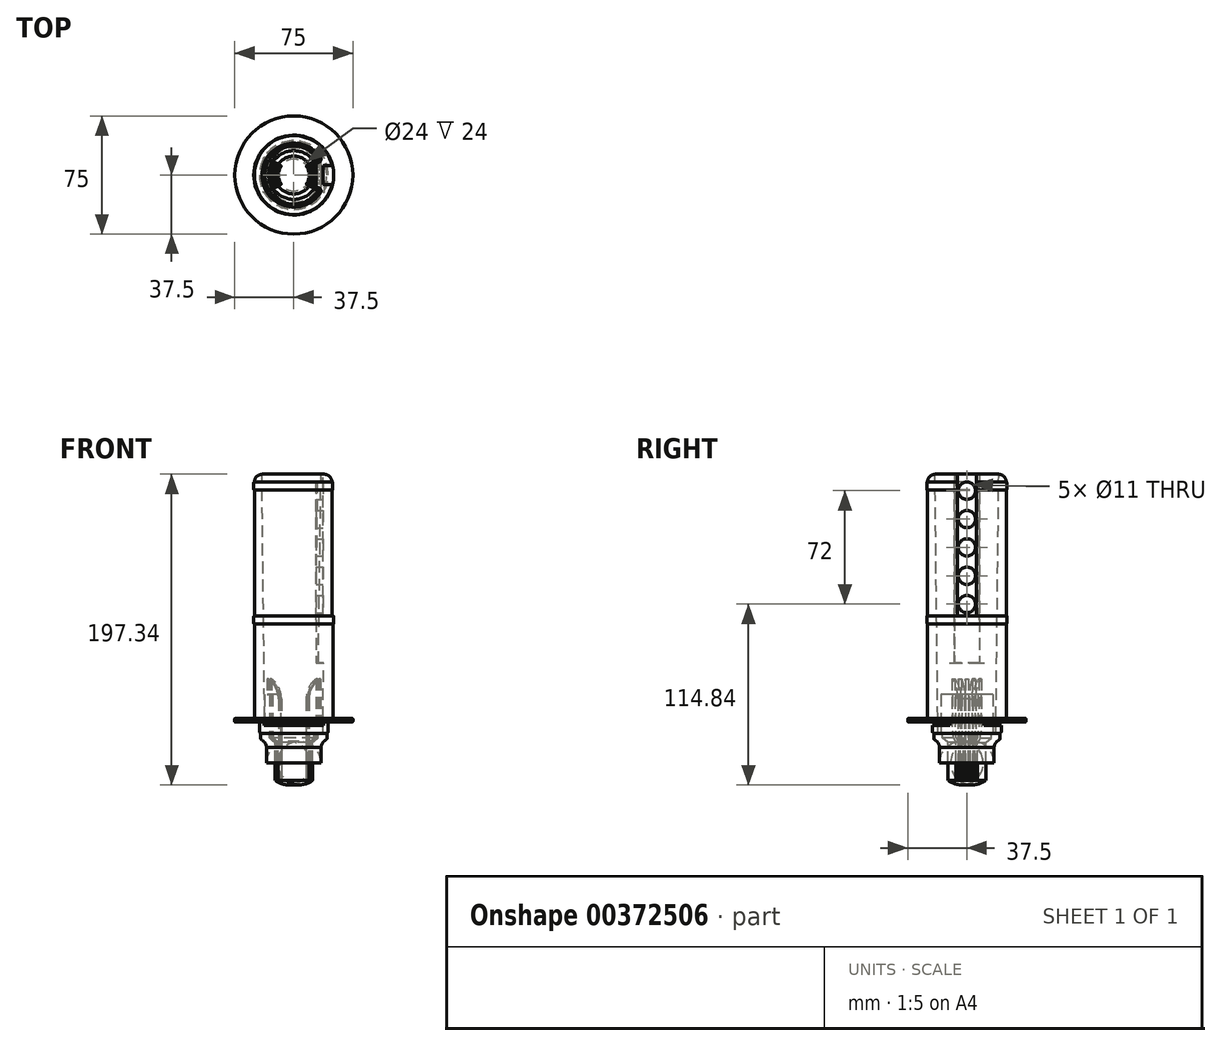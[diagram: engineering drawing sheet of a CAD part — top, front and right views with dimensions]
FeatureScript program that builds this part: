
annotation { "Feature Type Name" : "Feature", "Feature Type Description" : "" }
export const myFeature = defineFeature(function(context is Context, id is Id, definition is map)
    precondition{}
    {
        {
            var Q0;
            Q0=qCreatedBy(makeId("Front.planeOp"),FACE);
            var sketch = newSketch(context, id + "F0", { "sketchPlane" : qUnion([Q0])});
            skLineSegment(sketch, "E0", {"start": v(0, 155) * mm, "end": v(0, -40) * mm});
            skLineSegment(sketch, "E1", {"start": v(0, 155) * mm, "end": v(25, 155) * mm});
            skLineSegment(sketch, "E2", {"start": v(25, 155) * mm, "end": v(25, 150) * mm});
            skLineSegment(sketch, "E3", {"start": v(25, 150) * mm, "end": v(25.4, 150) * mm});
            skLineSegment(sketch, "E4", {"start": v(25.4, 150) * mm, "end": v(25.4, 145) * mm});
            skLineSegment(sketch, "E5", {"start": v(25.4, 145) * mm, "end": v(25, 145) * mm});
            skLineSegment(sketch, "E6", {"start": v(25, 145) * mm, "end": v(25, 65) * mm});
            skLineSegment(sketch, "E7", {"start": v(25, 65) * mm, "end": v(25.4, 65) * mm});
            skLineSegment(sketch, "E8", {"start": v(25.4, 65) * mm, "end": v(25.4, 60) * mm});
            skLineSegment(sketch, "E9", {"start": v(25.4, 60) * mm, "end": v(25, 60) * mm});
            skLineSegment(sketch, "E10", {"start": v(25, 60) * mm, "end": v(25, 0) * mm});
            skLineSegment(sketch, "E11", {"start": v(25, 0) * mm, "end": v(27.5, 0) * mm});
            skLineSegment(sketch, "E12", {"start": v(27.5, 0) * mm, "end": v(27.5, -2.5) * mm});
            skLineSegment(sketch, "E13", {"start": v(27.5, -2.5) * mm, "end": v(19.5, -2.5) * mm});
            skLineSegment(sketch, "E14", {"start": v(19.5, -2.5) * mm, "end": v(19.5, -4.5) * mm});
            skLineSegment(sketch, "E15", {"start": v(19.5, -4.5) * mm, "end": v(21.8, -4.5) * mm});
            skLineSegment(sketch, "E16", {"start": v(21.8, -4.5) * mm, "end": v(21.8, -9.5) * mm});
            skLineSegment(sketch, "E17", {"start": v(21.8, -9.5) * mm, "end": v(21, -9.5) * mm});
            skLineSegment(sketch, "E18", {"start": v(21, -9.5) * mm, "end": v(21, -13.5) * mm});
            skLineSegment(sketch, "E19", {"start": v(17.3, -18.5) * mm, "end": v(17.3, -28.5) * mm});
            skLineSegment(sketch, "E20", {"start": v(12, -39.39) * mm, "end": v(0, -39.39) * mm});
            skArc(sketch, "E21", {"start": v(21, -13.5) * mm, "mid": v(18.43, -15.47) * mm, "end": v(17.3, -18.5) * mm});
            skPoint(sketch, "E22.orphan", {"position": v(17.3, -13.5) * mm});
            skPoint(sketch, "E23.start.orphan", {"position": v(12, -28.39) * mm});
            skLineSegment(sketch, "E24", {"start": v(0, 155) * mm, "end": v(20.25, 155) * mm});
            skLineSegment(sketch, "E25", {"start": v(20.25, 155) * mm, "end": v(18.5, 0) * mm});
            skLineSegment(sketch, "E26", {"start": v(18.5, 0) * mm, "end": v(18.5, -10) * mm});
            skLineSegment(sketch, "E27", {"start": v(12, -39.39) * mm, "end": v(12, -15.39) * mm});
            skLineSegment(sketch, "E28", {"start": v(12, -15.39) * mm, "end": v(15.5, -12.49) * mm});
            skArc(sketch, "E29", {"start": v(12, -39.39) * mm, "mid": v(15.9, -34.56) * mm, "end": v(17.3, -28.5) * mm});
            skLineSegment(sketch, "E30", {"start": v(18.5, -10) * mm, "end": v(15.5, -10) * mm});
            skLineSegment(sketch, "E31", {"start": v(15.5, -10) * mm, "end": v(15.5, -12.49) * mm});
            skLineSegment(sketch, "E32", {"start": v(12, -39.39) * mm, "end": v(42.32, -39.39) * mm});
            skLineSegment(sketch, "E33", {"start": v(42.32, -39.39) * mm, "end": v(42.32, -10.56) * mm});
            skLineSegment(sketch, "E34", {"start": v(42.32, -10.56) * mm, "end": v(21, -10.56) * mm});
            skLineSegment(sketch, "E35", {"start": v(27.5, 0) * mm, "end": v(37.5, 0) * mm});
            skLineSegment(sketch, "E36", {"start": v(37.5, 0) * mm, "end": v(37.5, -2.5) * mm});
            skLineSegment(sketch, "E37", {"start": v(37.5, -2.5) * mm, "end": v(27.5, -2.5) * mm});
            skSolve(sketch);
        }
        {
            var Q0;
            {var subQ5=sQuery(id+"F0.wireOp",EDGE,"E2");Q0=makeQuery(id+"F0.imprint","IMPRINT",FACE,{"disambiguationData":[TD([[makeQuery(id+"F0.imprint","IMPRINT",EDGE,{"derivedFrom":subQ5}),-1.0]])]});}
            var Q1;
            Q1=sQuery(id+"F0.wireOp",EDGE,"E0");
            revolve(context, id + "F1", {"entities" : qUnion([Q0]), "axis" : qUnion([Q1]), "revolveType" : RevolveType.FULL});
        }
        {
            var Q0;
            Q0=makeQuery(id+"F1.opRevolve","SWEPT_FACE",FACE,{"disambiguationData":[OSD([sQuery(id+"F0.wireOp",EDGE,"E30")])]});
            var sketch = newSketch(context, id + "F2", { "sketchPlane" : qUnion([Q0])});
            skArc(sketch, "E38", {"start": v(-8.37, 16.5) * mm, "mid": v(-15.5, 0) * mm, "end": v(-8.37, -16.5) * mm});
            skArc(sketch, "E39", {"start": v(8.37, -16.5) * mm, "mid": v(15.5, 0) * mm, "end": v(8.37, 16.5) * mm});
            skSolve(sketch);
        }
        {
            var Q0;
            {var subQ0=sQuery(id+"F2.wireOp",EDGE,"E38");var subQ1=sQuery(id+"F0.wireOp",EDGE,"E30");var subQ2=makeQuery(id+"F1.opRevolve","SWEPT_EDGE",EDGE,{"disambiguationData":[OSD([sQuery(id+"F0.wireOp",EDGE,"E26"),subQ1])]});var subQ3=makeQuery(id+"F2.imprint","INTERSECT",VERTEX,{"disambiguationData":[OD(0.0)],"derivedFrom":[subQ2,subQ0]});Q0=makeQuery(id+"F2.imprint","IMPRINT",FACE,{"disambiguationData":[TD([[makeQuery(id+"F2.imprint","IMPRINT",EDGE,{"disambiguationData":[TD([[subQ3,-1.0]])],"derivedFrom":subQ0}),-1.0]])]});}
            var Q1;
            {var subQ0=sQuery(id+"F2.wireOp",EDGE,"E39");var subQ1=sQuery(id+"F0.wireOp",EDGE,"E30");var subQ2=makeQuery(id+"F1.opRevolve","SWEPT_EDGE",EDGE,{"disambiguationData":[OSD([sQuery(id+"F0.wireOp",EDGE,"E26"),subQ1])]});var subQ3=makeQuery(id+"F2.imprint","INTERSECT",VERTEX,{"disambiguationData":[OD(0.0)],"derivedFrom":[subQ2,subQ0]});Q1=makeQuery(id+"F2.imprint","IMPRINT",FACE,{"disambiguationData":[TD([[makeQuery(id+"F2.imprint","IMPRINT",EDGE,{"disambiguationData":[TD([[subQ3,-1.0]])],"derivedFrom":subQ0}),-1.0]])]});}
            extrude(context, id + "F3", {"entities" : qUnion([Q0, Q1]), "operationType" : NewBodyOperationType.ADD, "offsetDistance" : 25 * mm, "depth" : 25 * mm});
        }
        {
            var Q0;
            Q0=makeQuery(id+"F0.imprint","IMPRINT",FACE,{"disambiguationData":[TD([[makeQuery(id+"F0.imprint","IMPRINT",EDGE,{"derivedFrom":sQuery(id+"F0.wireOp",EDGE,"E19")}),1.0]])]});
            var Q1;
            Q1=makeQuery(id+"F1.opRevolve","SWEPT_FACE",FACE,{"disambiguationData":[OSD([sQuery(id+"F0.wireOp",EDGE,"E10")])]});
            revolve(context, id + "F4", {"operationType" : NewBodyOperationType.REMOVE, "entities" : qUnion([Q0]), "axis" : qUnion([Q1]), "revolveType" : RevolveType.FULL, "oppositeDirection" : true});
        }
        {
            var Q0;
            Q0=makeQuery(id+"F1.opRevolve","SWEPT_FACE",FACE,{"disambiguationData":[OSD([sQuery(id+"F0.wireOp",EDGE,"E1")])]});
            var sketch = newSketch(context, id + "F5", { "sketchPlane" : qUnion([Q0])});
            skLineSegment(sketch, "E40", {"start": v(25, 0) * mm, "end": v(23.69, 0) * mm});
            skLineSegment(sketch, "E41", {"start": v(14, 0) * mm, "end": v(14, -8) * mm});
            skLineSegment(sketch, "E42", {"start": v(14, -8) * mm, "end": v(23.69, -8) * mm});
            skLineSegment(sketch, "E43", {"start": v(14, 0) * mm, "end": v(14, 8) * mm});
            skLineSegment(sketch, "E44", {"start": v(14, 8) * mm, "end": v(23.69, 8) * mm});
            skLineSegment(sketch, "E45", {"start": v(23.69, 8) * mm, "end": v(23.69, 6) * mm});
            skLineSegment(sketch, "E46", {"start": v(23.69, -6) * mm, "end": v(24.27, -6) * mm});
            skLineSegment(sketch, "E47", {"start": v(23.69, 6) * mm, "end": v(24.27, 6) * mm});
            skLineSegment(sketch, "E48", {"start": v(24.27, -6) * mm, "end": v(26.6, -6) * mm});
            skLineSegment(sketch, "E49", {"start": v(26.6, -6) * mm, "end": v(26.6, 6) * mm});
            skLineSegment(sketch, "E50", {"start": v(26.6, 6) * mm, "end": v(24.27, 6) * mm});
            skLineSegment(sketch, "E51.trimOffspring", {"start": v(23.69, -6) * mm, "end": v(23.69, -8) * mm});
            skLineSegment(sketch, "E52", {"start": v(23.69, -6) * mm, "end": v(20.27, -6) * mm});
            skLineSegment(sketch, "E53", {"start": v(20.27, -6) * mm, "end": v(20.27, 6) * mm});
            skLineSegment(sketch, "E54", {"start": v(20.27, 6) * mm, "end": v(23.69, 6) * mm});
            skSolve(sketch);
        }
        {
            var Q0;
            {var subQ0=sQuery(id+"F5.wireOp",EDGE,"E40");var subQ1=sQuery(id+"F0.wireOp",EDGE,"E1");var subQ2=makeQuery(id+"F1.opRevolve","SWEPT_EDGE",EDGE,{"disambiguationData":[OSD([subQ1,sQuery(id+"F0.wireOp",EDGE,"E2")])]});var subQ3=makeQuery(id+"F5.imprint","INTERSECT",VERTEX,{"derivedFrom":[subQ2,subQ0]});Q0=makeQuery(id+"F5.imprint","IMPRINT",FACE,{"disambiguationData":[TD([[makeQuery(id+"F5.imprint","IMPRINT",EDGE,{"disambiguationData":[TD([[subQ3,-1.0]])],"derivedFrom":subQ0}),-1.0]])]});}
            var Q1;
            {var subQ0=sQuery(id+"F5.wireOp",EDGE,"E43");Q1=makeQuery(id+"F5.imprint","IMPRINT",FACE,{"disambiguationData":[TD([[makeQuery(id+"F5.imprint","IMPRINT",EDGE,{"derivedFrom":subQ0}),-1.0]])]});}
            var Q2;
            {var subQ0=sQuery(id+"F5.wireOp",EDGE,"E41");Q2=makeQuery(id+"F5.imprint","IMPRINT",FACE,{"disambiguationData":[TD([[makeQuery(id+"F5.imprint","IMPRINT",EDGE,{"derivedFrom":subQ0}),1.0]])]});}
            var Q3;
            {var subQ0=sQuery(id+"F5.wireOp",EDGE,"E40");var subQ1=sQuery(id+"F0.wireOp",EDGE,"E1");var subQ2=makeQuery(id+"F1.opRevolve","SWEPT_EDGE",EDGE,{"disambiguationData":[OSD([subQ1,sQuery(id+"F0.wireOp",EDGE,"E2")])]});var subQ3=makeQuery(id+"F5.imprint","INTERSECT",VERTEX,{"derivedFrom":[subQ2,subQ0]});Q3=makeQuery(id+"F5.imprint","IMPRINT",FACE,{"disambiguationData":[TD([[makeQuery(id+"F5.imprint","IMPRINT",EDGE,{"disambiguationData":[TD([[subQ3,-1.0]])],"derivedFrom":subQ0}),1.0]])]});}
            extrude(context, id + "F6", {"entities" : qUnion([Q0, Q1, Q2, Q3]), "operationType" : NewBodyOperationType.ADD, "oppositeDirection" : true, "depth" : 120 * mm});
        }
        {
            var Q0;
            {var subQ3=sQuery(id+"F5.wireOp",EDGE,"E48");Q0=makeQuery(id+"F5.imprint","IMPRINT",FACE,{"disambiguationData":[TD([[makeQuery(id+"F5.imprint","IMPRINT",EDGE,{"derivedFrom":subQ3}),1.0]])]});}
            var Q1;
            {var subQ3=sQuery(id+"F5.wireOp",EDGE,"29Uc3Rk1-qTzH-c9HX-FljC-5hYWEdNYT9Md");Q1=makeQuery(id+"F5.imprint","IMPRINT",FACE,{"disambiguationData":[TD([[makeQuery(id+"F5.imprint","IMPRINT",EDGE,{"derivedFrom":subQ3}),1.0]])]});}
            var Q2;
            {var subQ5=sQuery(id+"F5.wireOp",EDGE,"E47");Q2=makeQuery(id+"F5.imprint","IMPRINT",FACE,{"disambiguationData":[TD([[makeQuery(id+"F5.imprint","IMPRINT",EDGE,{"derivedFrom":subQ5}),-1.0]])]});}
            extrude(context, id + "F7", {"entities" : qUnion([Q0, Q1, Q2]), "operationType" : NewBodyOperationType.REMOVE, "oppositeDirection" : true, "depth" : 90 * mm});
        }
        {
            var Q0;
            Q0=makeQuery(id+"F7.boolean.opBoolean","COPY",FACE,{"derivedFrom":makeQuery(id+"F7.opExtrude","SWEPT_FACE",FACE,{"disambiguationData":[OSD([sQuery(id+"F5.wireOp",EDGE,"E53")])]})});
            var sketch = newSketch(context, id + "F8", { "sketchPlane" : qUnion([Q0])});
            skCircle(sketch, "E55", {"center": v(0, 144.5) * mm, "radius": 5.5 * mm});
            skPoint(sketch, "E56", {"position": v(0, 155) * mm});
            skCircle(sketch, "E57.0.1.0", {"center": v(0, 126.5) * mm, "radius": 5.5 * mm});
            skCircle(sketch, "E57.0.2.0", {"center": v(0, 108.5) * mm, "radius": 5.5 * mm});
            skCircle(sketch, "E57.0.3.0", {"center": v(0, 90.5) * mm, "radius": 5.5 * mm});
            skCircle(sketch, "E57.0.4.0", {"center": v(0, 72.5) * mm, "radius": 5.5 * mm});
            skLineSegment(sketch, "E57.direction1", {"start": v(0, 144.5) * mm, "end": v(25, 144.5) * mm, "construction": true});
            skLineSegment(sketch, "E57.direction2", {"start": v(0, 144.5) * mm, "end": v(0, 126.5) * mm, "construction": true});
            skSolve(sketch);
        }
        {
            var Q0;
            Q0=makeQuery(id+"F8.imprint","IMPRINT",FACE,{"disambiguationData":[TD([[makeQuery(id+"F8.imprint","IMPRINT",EDGE,{"derivedFrom":sQuery(id+"F8.wireOp",EDGE,"E57.0.4.0")}),1.0]])]});
            var Q1;
            Q1=makeQuery(id+"F8.imprint","IMPRINT",FACE,{"disambiguationData":[TD([[makeQuery(id+"F8.imprint","IMPRINT",EDGE,{"derivedFrom":sQuery(id+"F8.wireOp",EDGE,"E57.0.3.0")}),1.0]])]});
            var Q2;
            Q2=makeQuery(id+"F8.imprint","IMPRINT",FACE,{"disambiguationData":[TD([[makeQuery(id+"F8.imprint","IMPRINT",EDGE,{"derivedFrom":sQuery(id+"F8.wireOp",EDGE,"E57.0.2.0")}),1.0]])]});
            var Q3;
            Q3=makeQuery(id+"F8.imprint","IMPRINT",FACE,{"disambiguationData":[TD([[makeQuery(id+"F8.imprint","IMPRINT",EDGE,{"derivedFrom":sQuery(id+"F8.wireOp",EDGE,"E57.0.1.0")}),1.0]])]});
            var Q4;
            Q4=makeQuery(id+"F8.imprint","IMPRINT",FACE,{"disambiguationData":[TD([[makeQuery(id+"F8.imprint","IMPRINT",EDGE,{"derivedFrom":sQuery(id+"F8.wireOp",EDGE,"E55")}),1.0]])]});
            extrude(context, id + "F9", {"entities" : qUnion([Q0, Q1, Q2, Q3, Q4]), "operationType" : NewBodyOperationType.REMOVE, "oppositeDirection" : true, "depth" : 13 * mm, "hasSecondDirection" : true, "secondDirectionOppositeDirection" : false, "secondDirectionDepth" : 3 * mm});
        }
        {
            var Q0;
            Q0=makeQuery(id+"F1.opRevolve","SWEPT_FACE",FACE,{"disambiguationData":[OSD([sQuery(id+"F0.wireOp",EDGE,"E13")])]});
            var sketch = newSketch(context, id + "F10", { "sketchPlane" : qUnion([Q0])});
            skLineSegment(sketch, "E58", {"start": v(-27.5, 0) * mm, "end": v(-15, 0) * mm});
            skLineSegment(sketch, "E59", {"start": v(-15, 0) * mm, "end": v(-15, -11) * mm});
            skLineSegment(sketch, "E60", {"start": v(-15, -11) * mm, "end": v(-19.63, -11) * mm});
            skLineSegment(sketch, "E61", {"start": v(-22.5, -0.5) * mm, "end": v(-22.5, 0) * mm});
            skLineSegment(sketch, "E62", {"start": v(-19.68, 10.9) * mm, "end": v(-15, 11) * mm});
            skLineSegment(sketch, "E63", {"start": v(-15, 11) * mm, "end": v(-15, 0) * mm});
            skLineSegment(sketch, "E64.MirrorCS", {"start": v(15, 11) * mm, "end": v(15, 0) * mm});
            skLineSegment(sketch, "E65.MirrorCS", {"start": v(19.68, 10.9) * mm, "end": v(15, 11) * mm});
            skLineSegment(sketch, "E66.MirrorCS", {"start": v(15, -11) * mm, "end": v(19.63, -11) * mm});
            skLineSegment(sketch, "E67.MirrorCS", {"start": v(15, 0) * mm, "end": v(15, -11) * mm});
            skCircle(sketch, "E68", {"center": v(0, 0) * mm, "radius": 22.5 * mm});
            skCircle(sketch, "E69", {"center": v(0, 0) * mm, "radius": 19.5 * mm});
            skPoint(sketch, "E70.orphan", {"position": v(-22.74, 10.83) * mm});
            skPoint(sketch, "E71.orphan", {"position": v(-22.26, -11) * mm});
            skPoint(sketch, "E72.orphan", {"position": v(22.26, -11) * mm});
            skPoint(sketch, "E73.MirrorCS.end.orphan", {"position": v(22.74, 10.83) * mm});
            skSolve(sketch);
        }
        {
            var Q0;
            {var subQ0=sQuery(id+"F10.wireOp",EDGE,"E68");var subQ1=sQuery(id+"F10.wireOp",EDGE,"E58");var subQ2=makeQuery(id+"F10.imprint","INTERSECT",VERTEX,{"derivedFrom":[subQ1,subQ0]});Q0=makeQuery(id+"F10.imprint","IMPRINT",FACE,{"disambiguationData":[TD([[makeQuery(id+"F10.imprint","IMPRINT",EDGE,{"disambiguationData":[TD([[subQ2,-1.0]])],"derivedFrom":subQ1}),1.0]])]});}
            var Q1;
            {var subQ0=sQuery(id+"F10.wireOp",EDGE,"E68");var subQ4=sQuery(id+"F10.wireOp",EDGE,"E58");var subQ5=makeQuery(id+"F10.imprint","INTERSECT",VERTEX,{"derivedFrom":[subQ4,subQ0]});Q1=makeQuery(id+"F10.imprint","IMPRINT",FACE,{"disambiguationData":[TD([[makeQuery(id+"F10.imprint","IMPRINT",EDGE,{"disambiguationData":[TD([[subQ5,-1.0]])],"derivedFrom":subQ4}),-1.0]])]});}
            var Q2;
            {var subQ0=sQuery(id+"F10.wireOp",EDGE,"E68");var subQ1=sQuery(id+"F10.wireOp",EDGE,"E65.MirrorCS");var subQ2=makeQuery(id+"F10.imprint","INTERSECT",VERTEX,{"derivedFrom":[subQ1,subQ0]});Q2=makeQuery(id+"F10.imprint","IMPRINT",FACE,{"disambiguationData":[TD([[makeQuery(id+"F10.imprint","IMPRINT",EDGE,{"disambiguationData":[TD([[subQ2,-1.0]])],"derivedFrom":subQ1}),1.0]])]});}
            extrude(context, id + "F11", {"entities" : qUnion([Q0, Q1, Q2]), "operationType" : NewBodyOperationType.ADD, "depth" : 3 * mm});
        }
        {
            var Q0;
            Q0=makeQuery(id+"F6.boolean.opBoolean","INTERSECT",EDGE,{"derivedFrom":[makeQuery(id+"F1.opRevolve","SWEPT_FACE",FACE,{"disambiguationData":[OSD([sQuery(id+"F0.wireOp",EDGE,"E25")])]}),makeQuery(id+"F6.opExtrude","SWEPT_FACE",FACE,{"disambiguationData":[OSD([sQuery(id+"F5.wireOp",EDGE,"E44")])]})]});
            var Q1;
            Q1=makeQuery(id+"F6.boolean.opBoolean","INTERSECT",EDGE,{"derivedFrom":[makeQuery(id+"F1.opRevolve","SWEPT_FACE",FACE,{"disambiguationData":[OSD([sQuery(id+"F0.wireOp",EDGE,"E25")])]}),makeQuery(id+"F6.opExtrude","SWEPT_FACE",FACE,{"disambiguationData":[OSD([sQuery(id+"F5.wireOp",EDGE,"E42")])]})]});
            fillet(context, id + "F12", {"entities" : qUnion([Q0, Q1]), "radius" : 2 * mm, "tangentPropagation" : true, "allowEdgeOverflow" : false});
        }
        {
            var Q0;
            Q0=makeQuery(id+"F11.opExtrude","SWEPT_EDGE",EDGE,{"disambiguationData":[OSD([sQuery(id+"F10.wireOp",EDGE,"E66.MirrorCS"),sQuery(id+"F10.wireOp",EDGE,"E68")])]});
            var Q1;
            Q1=makeQuery(id+"F11.opExtrude","SWEPT_EDGE",EDGE,{"disambiguationData":[OSD([sQuery(id+"F10.wireOp",EDGE,"E66.MirrorCS"),sQuery(id+"F10.wireOp",EDGE,"E69")])]});
            var Q2;
            Q2=makeQuery(id+"F11.opExtrude","SWEPT_EDGE",EDGE,{"disambiguationData":[OSD([sQuery(id+"F10.wireOp",EDGE,"E65.MirrorCS"),sQuery(id+"F10.wireOp",EDGE,"E68")])]});
            var Q3;
            Q3=makeQuery(id+"F11.opExtrude","SWEPT_EDGE",EDGE,{"disambiguationData":[OSD([sQuery(id+"F10.wireOp",EDGE,"E65.MirrorCS"),sQuery(id+"F10.wireOp",EDGE,"E69")])]});
            var Q4;
            Q4=makeQuery(id+"F11.opExtrude","SWEPT_EDGE",EDGE,{"disambiguationData":[OSD([sQuery(id+"F10.wireOp",EDGE,"E62"),sQuery(id+"F10.wireOp",EDGE,"E69")])]});
            var Q5;
            Q5=makeQuery(id+"F11.opExtrude","SWEPT_EDGE",EDGE,{"disambiguationData":[OSD([sQuery(id+"F10.wireOp",EDGE,"E62"),sQuery(id+"F10.wireOp",EDGE,"E68")])]});
            var Q6;
            Q6=makeQuery(id+"F11.opExtrude","SWEPT_EDGE",EDGE,{"disambiguationData":[OSD([sQuery(id+"F10.wireOp",EDGE,"E60"),sQuery(id+"F10.wireOp",EDGE,"E68")])]});
            var Q7;
            Q7=makeQuery(id+"F11.opExtrude","SWEPT_EDGE",EDGE,{"disambiguationData":[OSD([sQuery(id+"F10.wireOp",EDGE,"E60"),sQuery(id+"F10.wireOp",EDGE,"E69")])]});
            fillet(context, id + "F13", {"entities" : qUnion([Q0, Q1, Q2, Q3, Q4, Q5, Q6, Q7]), "radius" : 2 * mm, "tangentPropagation" : true, "allowEdgeOverflow" : false});
        }
        {
            var Q0;
            Q0=makeQuery(id+"F1.opRevolve","SWEPT_EDGE",EDGE,{"disambiguationData":[OSD([sQuery(id+"F0.wireOp",EDGE,"E18"),sQuery(id+"F0.wireOp",EDGE,"E21")])]});
            var Q1;
            Q1=makeQuery(id+"F1.opRevolve","SWEPT_EDGE",EDGE,{"disambiguationData":[OSD([sQuery(id+"F0.wireOp",EDGE,"E16"),sQuery(id+"F0.wireOp",EDGE,"E17")])]});
            fillet(context, id + "F14", {"entities" : qUnion([Q0, Q1]), "radius" : 1 * mm, "tangentPropagation" : true, "allowEdgeOverflow" : false});
        }
        {
            var Q0;
            Q0=makeQuery(id+"F1.opRevolve","SWEPT_EDGE",EDGE,{"disambiguationData":[OSD([sQuery(id+"F0.wireOp",EDGE,"E1"),sQuery(id+"F0.wireOp",EDGE,"E2")])]});
            fillet(context, id + "F15", {"entities" : qUnion([Q0]), "radius" : 5 * mm, "tangentPropagation" : true, "allowEdgeOverflow" : false});
        }
        {
            var Q0;
            Q0=qCreatedBy(makeId("Right.planeOp"),FACE);
            var sketch = newSketch(context, id + "F16", { "sketchPlane" : qUnion([Q0])});
            skLineSegment(sketch, "E74", {"start": v(20.7, -2.5) * mm, "end": v(15, -2.5) * mm});
            skLineSegment(sketch, "E75", {"start": v(15, -2.5) * mm, "end": v(15, -4.46) * mm});
            skLineSegment(sketch, "E76", {"start": v(15, -4.46) * mm, "end": v(20.7, -4.46) * mm});
            skLineSegment(sketch, "E77", {"start": v(20.7, -4.46) * mm, "end": v(20.7, -2.5) * mm});
            skLineSegment(sketch, "E78.MirrorCS", {"start": v(-15, -2.5) * mm, "end": v(-15, -4.46) * mm});
            skLineSegment(sketch, "E79.MirrorCS", {"start": v(-20.7, -2.5) * mm, "end": v(-15, -2.5) * mm});
            skLineSegment(sketch, "E80.MirrorCS", {"start": v(-20.7, -4.46) * mm, "end": v(-20.7, -2.5) * mm});
            skLineSegment(sketch, "E81.MirrorCS", {"start": v(-15, -4.46) * mm, "end": v(-20.7, -4.46) * mm});
            skSolve(sketch);
        }
        {
            var Q0;
            Q0 = qSketchRegion(id + "F16", true);
            extrude(context, id + "F17", {"entities" : qUnion([Q0]), "operationType" : NewBodyOperationType.REMOVE, "depth" : 50 * mm, "hasSecondDirection" : true, "secondDirectionOppositeDirection" : true, "secondDirectionDepth" : 50 * mm});
        }
        {
            var Q0;
            {var subQ0=sQuery(id+"F0.wireOp",EDGE,"E1");Q0=makeQuery(id+"F6.boolean.opBoolean","MERGE",FACE,{"derivedFrom":[makeQuery(id+"F1.opRevolve","SWEPT_FACE",FACE,{"disambiguationData":[OSD([subQ0])]}),makeQuery(id+"F6.opExtrude","CAP_FACE",FACE,{"disambiguationData":[OSD([subQ0,sQuery(id+"F0.wireOp",EDGE,"E25"),sQuery(id+"F5.wireOp",EDGE,"E41"),sQuery(id+"F5.wireOp",EDGE,"E42"),sQuery(id+"F5.wireOp",EDGE,"E43"),sQuery(id+"F5.wireOp",EDGE,"E44")])],"isStart":true})]});}
            var sketch = newSketch(context, id + "F18", { "sketchPlane" : qUnion([Q0])});
            skLineSegment(sketch, "E82", {"start": v(20.68, 0) * mm, "end": v(20.68, 6) * mm});
            skLineSegment(sketch, "E83", {"start": v(20.68, 6) * mm, "end": v(18.68, 6) * mm});
            skLineSegment(sketch, "E84", {"start": v(18.68, 6) * mm, "end": v(18.68, -6) * mm});
            skLineSegment(sketch, "E85", {"start": v(18.68, -6) * mm, "end": v(20.68, -6) * mm});
            skLineSegment(sketch, "E86", {"start": v(20.68, -6) * mm, "end": v(20.68, 0) * mm});
            skSolve(sketch);
        }
        {
            var Q0;
            {var subQ2=sQuery(id+"F18.wireOp",EDGE,"E82");Q0=makeQuery(id+"F18.imprint","IMPRINT",FACE,{"disambiguationData":[TD([[makeQuery(id+"F18.imprint","IMPRINT",EDGE,{"derivedFrom":subQ2}),1.0]])]});}
            var Q1;
            {var subQ0=sQuery(id+"F18.wireOp",EDGE,"E84");Q1=makeQuery(id+"F18.imprint","IMPRINT",FACE,{"disambiguationData":[TD([[makeQuery(id+"F18.imprint","IMPRINT",EDGE,{"derivedFrom":subQ0}),1.0]])]});}
            extrude(context, id + "F19", {"entities" : qUnion([Q0, Q1]), "operationType" : NewBodyOperationType.REMOVE, "oppositeDirection" : true, "depth" : 90 * mm});
        }
        {
            var Q0;
            Q0=qCreatedBy(makeId("Top.planeOp"),FACE);
            var sketch = newSketch(context, id + "F20", { "sketchPlane" : qUnion([Q0])});
            skCircle(sketch, "E87", {"center": v(0, 0) * mm, "radius": 9.75 * mm});
            skSolve(sketch);
        }
        {
            var Q0;
            Q0=makeQuery(id+"F20.imprint","IMPRINT",FACE,{"disambiguationData":[TD([[makeQuery(id+"F20.imprint","IMPRINT",EDGE,{"derivedFrom":sQuery(id+"F20.wireOp",EDGE,"E87")}),1.0]])]});
            var sketch = newSketch(context, id + "F21", { "sketchPlane" : qUnion([Q0])});
            skLineSegment(sketch, "E88", {"start": v(-2.93, 0) * mm, "end": v(-2.93, 1) * mm});
            skLineSegment(sketch, "E89", {"start": v(-2.93, 0) * mm, "end": v(-2.93, -1) * mm});
            skLineSegment(sketch, "E90", {"start": v(-2.93, -1) * mm, "end": v(-16.95, -1) * mm});
            skLineSegment(sketch, "E91", {"start": v(-16.95, -1) * mm, "end": v(-16.95, 1) * mm});
            skLineSegment(sketch, "E92", {"start": v(-16.95, 1) * mm, "end": v(-2.93, 1) * mm});
            skPoint(sketch, "E93.start.orphan", {"position": v(-16.95, 0) * mm});
            skLineSegment(sketch, "E94.1.0", {"start": v(-16.63, -3.42) * mm, "end": v(-3.1, 0.2) * mm});
            skLineSegment(sketch, "E94.1.1", {"start": v(-2.83, -0.76) * mm, "end": v(-2.58, -1.73) * mm});
            skLineSegment(sketch, "E94.1.2", {"start": v(-2.83, -0.76) * mm, "end": v(-3.1, 0.2) * mm});
            skLineSegment(sketch, "E94.1.3", {"start": v(-2.58, -1.73) * mm, "end": v(-16.11, -5.35) * mm});
            skLineSegment(sketch, "E94.1.4", {"start": v(-16.11, -5.35) * mm, "end": v(-16.63, -3.42) * mm});
            skLineSegment(sketch, "E94.2.0", {"start": v(-15.18, -7.6) * mm, "end": v(-3.04, -0.6) * mm});
            skLineSegment(sketch, "E94.2.1", {"start": v(-2.54, -1.47) * mm, "end": v(-2.04, -2.33) * mm});
            skLineSegment(sketch, "E94.2.2", {"start": v(-2.54, -1.47) * mm, "end": v(-3.04, -0.6) * mm});
            skLineSegment(sketch, "E94.2.3", {"start": v(-2.04, -2.33) * mm, "end": v(-14.18, -9.34) * mm});
            skLineSegment(sketch, "E94.2.4", {"start": v(-14.18, -9.34) * mm, "end": v(-15.18, -7.6) * mm});
            skLineSegment(sketch, "E94.3.1", {"start": v(-2.07, -2.07) * mm, "end": v(-1.37, -2.78) * mm});
            skLineSegment(sketch, "E94.3.2", {"start": v(-2.07, -2.07) * mm, "end": v(-2.78, -1.37) * mm});
            skLineSegment(sketch, "E94.4.1", {"start": v(-1.47, -2.54) * mm, "end": v(-0.6, -3.04) * mm});
            skLineSegment(sketch, "E94.4.2", {"start": v(-1.47, -2.54) * mm, "end": v(-2.33, -2.04) * mm});
            skLineSegment(sketch, "E94.5.1", {"start": v(-0.76, -2.83) * mm, "end": v(0.2, -3.1) * mm});
            skLineSegment(sketch, "E94.5.2", {"start": v(-0.76, -2.83) * mm, "end": v(-1.73, -2.58) * mm});
            skLineSegment(sketch, "E94.6.1", {"start": v(0, -2.93) * mm, "end": v(1, -2.93) * mm});
            skLineSegment(sketch, "E94.6.2", {"start": v(0, -2.93) * mm, "end": v(-1, -2.93) * mm});
            skLineSegment(sketch, "E94.7.1", {"start": v(0.76, -2.83) * mm, "end": v(1.73, -2.58) * mm});
            skLineSegment(sketch, "E94.7.2", {"start": v(0.76, -2.83) * mm, "end": v(-0.2, -3.1) * mm});
            skLineSegment(sketch, "E94.8.1", {"start": v(1.47, -2.54) * mm, "end": v(2.33, -2.04) * mm});
            skLineSegment(sketch, "E94.8.2", {"start": v(1.47, -2.54) * mm, "end": v(0.6, -3.04) * mm});
            skLineSegment(sketch, "E94.9.1", {"start": v(2.07, -2.07) * mm, "end": v(2.78, -1.37) * mm});
            skLineSegment(sketch, "E94.9.2", {"start": v(2.07, -2.07) * mm, "end": v(1.37, -2.78) * mm});
            skLineSegment(sketch, "E94.10.0", {"start": v(14.18, -9.34) * mm, "end": v(2.04, -2.33) * mm});
            skLineSegment(sketch, "E94.10.1", {"start": v(2.54, -1.47) * mm, "end": v(3.04, -0.6) * mm});
            skLineSegment(sketch, "E94.10.2", {"start": v(2.54, -1.47) * mm, "end": v(2.04, -2.33) * mm});
            skLineSegment(sketch, "E94.10.3", {"start": v(3.04, -0.6) * mm, "end": v(15.18, -7.6) * mm});
            skLineSegment(sketch, "E94.10.4", {"start": v(15.18, -7.6) * mm, "end": v(14.18, -9.34) * mm});
            skLineSegment(sketch, "E94.11.0", {"start": v(16.11, -5.35) * mm, "end": v(2.58, -1.73) * mm});
            skLineSegment(sketch, "E94.11.1", {"start": v(2.83, -0.76) * mm, "end": v(3.1, 0.2) * mm});
            skLineSegment(sketch, "E94.11.2", {"start": v(2.83, -0.76) * mm, "end": v(2.58, -1.73) * mm});
            skLineSegment(sketch, "E94.11.3", {"start": v(3.1, 0.2) * mm, "end": v(16.63, -3.42) * mm});
            skLineSegment(sketch, "E94.11.4", {"start": v(16.63, -3.42) * mm, "end": v(16.11, -5.35) * mm});
            skLineSegment(sketch, "E94.12.0", {"start": v(16.95, -1) * mm, "end": v(2.93, -1) * mm});
            skLineSegment(sketch, "E94.12.1", {"start": v(2.93, 0) * mm, "end": v(2.93, 1) * mm});
            skLineSegment(sketch, "E94.12.2", {"start": v(2.93, 0) * mm, "end": v(2.93, -1) * mm});
            skLineSegment(sketch, "E94.12.3", {"start": v(2.93, 1) * mm, "end": v(16.95, 1) * mm});
            skLineSegment(sketch, "E94.12.4", {"start": v(16.95, 1) * mm, "end": v(16.95, -1) * mm});
            skLineSegment(sketch, "E94.13.0", {"start": v(16.63, 3.42) * mm, "end": v(3.1, -0.2) * mm});
            skLineSegment(sketch, "E94.13.1", {"start": v(2.83, 0.76) * mm, "end": v(2.58, 1.73) * mm});
            skLineSegment(sketch, "E94.13.2", {"start": v(2.83, 0.76) * mm, "end": v(3.1, -0.2) * mm});
            skLineSegment(sketch, "E94.13.3", {"start": v(2.58, 1.73) * mm, "end": v(16.11, 5.35) * mm});
            skLineSegment(sketch, "E94.13.4", {"start": v(16.11, 5.35) * mm, "end": v(16.63, 3.42) * mm});
            skLineSegment(sketch, "E94.14.0", {"start": v(15.18, 7.6) * mm, "end": v(3.04, 0.6) * mm});
            skLineSegment(sketch, "E94.14.1", {"start": v(2.54, 1.47) * mm, "end": v(2.04, 2.33) * mm});
            skLineSegment(sketch, "E94.14.2", {"start": v(2.54, 1.47) * mm, "end": v(3.04, 0.6) * mm});
            skLineSegment(sketch, "E94.14.3", {"start": v(2.04, 2.33) * mm, "end": v(14.18, 9.34) * mm});
            skLineSegment(sketch, "E94.14.4", {"start": v(14.18, 9.34) * mm, "end": v(15.18, 7.6) * mm});
            skLineSegment(sketch, "E94.15.1", {"start": v(2.07, 2.07) * mm, "end": v(1.37, 2.78) * mm});
            skLineSegment(sketch, "E94.15.2", {"start": v(2.07, 2.07) * mm, "end": v(2.78, 1.37) * mm});
            skLineSegment(sketch, "E94.16.1", {"start": v(1.47, 2.54) * mm, "end": v(0.6, 3.04) * mm});
            skLineSegment(sketch, "E94.16.2", {"start": v(1.47, 2.54) * mm, "end": v(2.33, 2.04) * mm});
            skLineSegment(sketch, "E94.17.1", {"start": v(0.76, 2.83) * mm, "end": v(-0.2, 3.1) * mm});
            skLineSegment(sketch, "E94.17.2", {"start": v(0.76, 2.83) * mm, "end": v(1.73, 2.58) * mm});
            skLineSegment(sketch, "E94.18.1", {"start": v(0, 2.93) * mm, "end": v(-1, 2.93) * mm});
            skLineSegment(sketch, "E94.18.2", {"start": v(0, 2.93) * mm, "end": v(1, 2.93) * mm});
            skLineSegment(sketch, "E94.19.1", {"start": v(-0.76, 2.83) * mm, "end": v(-1.73, 2.58) * mm});
            skLineSegment(sketch, "E94.19.2", {"start": v(-0.76, 2.83) * mm, "end": v(0.2, 3.1) * mm});
            skLineSegment(sketch, "E94.20.1", {"start": v(-1.47, 2.54) * mm, "end": v(-2.33, 2.04) * mm});
            skLineSegment(sketch, "E94.20.2", {"start": v(-1.47, 2.54) * mm, "end": v(-0.6, 3.04) * mm});
            skLineSegment(sketch, "E94.20.3", {"start": v(-2.33, 2.04) * mm, "end": v(-2.73, 2.73) * mm});
            skLineSegment(sketch, "E94.21.1", {"start": v(-2.07, 2.07) * mm, "end": v(-2.78, 1.37) * mm});
            skLineSegment(sketch, "E94.21.2", {"start": v(-2.07, 2.07) * mm, "end": v(-1.37, 2.78) * mm});
            skLineSegment(sketch, "E94.22.0", {"start": v(-14.18, 9.34) * mm, "end": v(-2.04, 2.33) * mm});
            skLineSegment(sketch, "E94.22.1", {"start": v(-2.54, 1.47) * mm, "end": v(-3.04, 0.6) * mm});
            skLineSegment(sketch, "E94.22.2", {"start": v(-2.54, 1.47) * mm, "end": v(-2.04, 2.33) * mm});
            skLineSegment(sketch, "E94.22.3", {"start": v(-3.04, 0.6) * mm, "end": v(-15.18, 7.6) * mm});
            skLineSegment(sketch, "E94.22.4", {"start": v(-15.18, 7.6) * mm, "end": v(-14.18, 9.34) * mm});
            skLineSegment(sketch, "E94.23.0", {"start": v(-16.11, 5.35) * mm, "end": v(-2.58, 1.73) * mm});
            skLineSegment(sketch, "E94.23.1", {"start": v(-2.83, 0.76) * mm, "end": v(-3.1, -0.2) * mm});
            skLineSegment(sketch, "E94.23.2", {"start": v(-2.83, 0.76) * mm, "end": v(-2.58, 1.73) * mm});
            skLineSegment(sketch, "E94.23.3", {"start": v(-3.1, -0.2) * mm, "end": v(-16.63, 3.42) * mm});
            skLineSegment(sketch, "E94.23.4", {"start": v(-16.63, 3.42) * mm, "end": v(-16.11, 5.35) * mm});
            skPoint(sketch, "E94.center", {"position": v(0, 0) * mm});
            skPoint(sketch, "E95.orphan", {"position": v(-7.6, 15.18) * mm});
            skPoint(sketch, "E96.orphan", {"position": v(-9.34, 14.18) * mm});
            skSolve(sketch);
        }
        {
            var Q0;
            {var subQ0=sQuery(id+"F21.wireOp",EDGE,"E94.2.4");Q0=makeQuery(id+"F21.imprint","IMPRINT",FACE,{"disambiguationData":[TD([[makeQuery(id+"F21.imprint","IMPRINT",EDGE,{"derivedFrom":subQ0}),-1.0]])]});}
            var Q1;
            {var subQ0=sQuery(id+"F21.wireOp",EDGE,"E94.1.4");Q1=makeQuery(id+"F21.imprint","IMPRINT",FACE,{"disambiguationData":[TD([[makeQuery(id+"F21.imprint","IMPRINT",EDGE,{"derivedFrom":subQ0}),-1.0]])]});}
            var Q2;
            {var subQ0=sQuery(id+"F21.wireOp",EDGE,"E91");Q2=makeQuery(id+"F21.imprint","IMPRINT",FACE,{"disambiguationData":[TD([[makeQuery(id+"F21.imprint","IMPRINT",EDGE,{"derivedFrom":subQ0}),-1.0]])]});}
            var Q3;
            {var subQ0=sQuery(id+"F21.wireOp",EDGE,"E94.23.4");Q3=makeQuery(id+"F21.imprint","IMPRINT",FACE,{"disambiguationData":[TD([[makeQuery(id+"F21.imprint","IMPRINT",EDGE,{"derivedFrom":subQ0}),-1.0]])]});}
            var Q4;
            {var subQ0=sQuery(id+"F21.wireOp",EDGE,"E94.22.4");Q4=makeQuery(id+"F21.imprint","IMPRINT",FACE,{"disambiguationData":[TD([[makeQuery(id+"F21.imprint","IMPRINT",EDGE,{"derivedFrom":subQ0}),-1.0]])]});}
            var Q5;
            {var subQ0=sQuery(id+"F21.wireOp",EDGE,"E94.10.4");Q5=makeQuery(id+"F21.imprint","IMPRINT",FACE,{"disambiguationData":[TD([[makeQuery(id+"F21.imprint","IMPRINT",EDGE,{"derivedFrom":subQ0}),-1.0]])]});}
            var Q6;
            {var subQ0=sQuery(id+"F21.wireOp",EDGE,"E94.11.4");Q6=makeQuery(id+"F21.imprint","IMPRINT",FACE,{"disambiguationData":[TD([[makeQuery(id+"F21.imprint","IMPRINT",EDGE,{"derivedFrom":subQ0}),-1.0]])]});}
            var Q7;
            {var subQ0=sQuery(id+"F21.wireOp",EDGE,"E94.12.4");Q7=makeQuery(id+"F21.imprint","IMPRINT",FACE,{"disambiguationData":[TD([[makeQuery(id+"F21.imprint","IMPRINT",EDGE,{"derivedFrom":subQ0}),-1.0]])]});}
            var Q8;
            {var subQ0=sQuery(id+"F21.wireOp",EDGE,"E94.13.4");Q8=makeQuery(id+"F21.imprint","IMPRINT",FACE,{"disambiguationData":[TD([[makeQuery(id+"F21.imprint","IMPRINT",EDGE,{"derivedFrom":subQ0}),-1.0]])]});}
            var Q9;
            {var subQ0=sQuery(id+"F21.wireOp",EDGE,"E94.14.4");Q9=makeQuery(id+"F21.imprint","IMPRINT",FACE,{"disambiguationData":[TD([[makeQuery(id+"F21.imprint","IMPRINT",EDGE,{"derivedFrom":subQ0}),-1.0]])]});}
            extrude(context, id + "F22", {"entities" : qUnion([Q0, Q1, Q2, Q3, Q4, Q5, Q6, Q7, Q8, Q9]), "operationType" : NewBodyOperationType.ADD, "depth" : 25 * mm, "hasSecondDirection" : true, "secondDirectionOppositeDirection" : true, "secondDirectionDepth" : 39.35 * mm});
        }
        {
            var Q0;
            Q0=makeQuery(id+"F0.imprint","IMPRINT",FACE,{"disambiguationData":[TD([[makeQuery(id+"F0.imprint","IMPRINT",EDGE,{"derivedFrom":sQuery(id+"F0.wireOp",EDGE,"E19")}),1.0]])]});
            var Q1;
            Q1=makeQuery(id+"F1.opRevolve","SWEPT_FACE",FACE,{"disambiguationData":[OSD([sQuery(id+"F0.wireOp",EDGE,"E29")])]});
            revolve(context, id + "F23", {"operationType" : NewBodyOperationType.REMOVE, "entities" : qUnion([Q0]), "axis" : qUnion([Q1]), "revolveType" : RevolveType.FULL, "oppositeDirection" : true});
        }
        {
            var Q0;
            {var subQ0=sQuery(id+"F20.wireOp",EDGE,"E87");var subQ1=makeQuery(id+"F20.imprint","IMPRINT",EDGE,{"derivedFrom":subQ0});Q0=makeQuery(id+"F22.opExtrude","CAP_EDGE",EDGE,{"disambiguationData":[OSD([subQ0]),TDD([makeQuery(id+"F21.imprint","IMPRINT",EDGE,{"disambiguationData":[TD([[makeQuery(id+"F21.imprint","INTERSECT",VERTEX,{"derivedFrom":[subQ1,sQuery(id+"F21.wireOp",EDGE,"E94.10.0")]}),-1.0]])],"derivedFrom":subQ1})])],"isStart":false});}
            var Q1;
            {var subQ0=sQuery(id+"F20.wireOp",EDGE,"E87");var subQ1=makeQuery(id+"F20.imprint","IMPRINT",EDGE,{"derivedFrom":subQ0});Q1=makeQuery(id+"F22.opExtrude","CAP_EDGE",EDGE,{"disambiguationData":[OSD([subQ0]),TDD([makeQuery(id+"F21.imprint","IMPRINT",EDGE,{"disambiguationData":[TD([[makeQuery(id+"F21.imprint","INTERSECT",VERTEX,{"derivedFrom":[subQ1,sQuery(id+"F21.wireOp",EDGE,"E94.11.0")]}),-1.0]])],"derivedFrom":subQ1})])],"isStart":false});}
            var Q2;
            {var subQ0=sQuery(id+"F20.wireOp",EDGE,"E87");var subQ1=makeQuery(id+"F20.imprint","IMPRINT",EDGE,{"derivedFrom":subQ0});Q2=makeQuery(id+"F22.opExtrude","CAP_EDGE",EDGE,{"disambiguationData":[OSD([subQ0]),TDD([makeQuery(id+"F21.imprint","IMPRINT",EDGE,{"disambiguationData":[TD([[makeQuery(id+"F21.imprint","INTERSECT",VERTEX,{"derivedFrom":[subQ1,sQuery(id+"F21.wireOp",EDGE,"E94.12.0")]}),-1.0]])],"derivedFrom":subQ1})])],"isStart":false});}
            var Q3;
            {var subQ0=sQuery(id+"F20.wireOp",EDGE,"E87");var subQ1=makeQuery(id+"F20.imprint","IMPRINT",EDGE,{"derivedFrom":subQ0});Q3=makeQuery(id+"F22.opExtrude","CAP_EDGE",EDGE,{"disambiguationData":[OSD([subQ0]),TDD([makeQuery(id+"F21.imprint","IMPRINT",EDGE,{"disambiguationData":[TD([[makeQuery(id+"F21.imprint","INTERSECT",VERTEX,{"derivedFrom":[subQ1,sQuery(id+"F21.wireOp",EDGE,"E94.13.0")]}),-1.0]])],"derivedFrom":subQ1})])],"isStart":false});}
            var Q4;
            {var subQ0=sQuery(id+"F20.wireOp",EDGE,"E87");var subQ1=makeQuery(id+"F20.imprint","IMPRINT",EDGE,{"derivedFrom":subQ0});Q4=makeQuery(id+"F22.opExtrude","CAP_EDGE",EDGE,{"disambiguationData":[OSD([subQ0]),TDD([makeQuery(id+"F21.imprint","IMPRINT",EDGE,{"disambiguationData":[TD([[makeQuery(id+"F21.imprint","INTERSECT",VERTEX,{"derivedFrom":[subQ1,sQuery(id+"F21.wireOp",EDGE,"E94.14.0")]}),-1.0]])],"derivedFrom":subQ1})])],"isStart":false});}
            var Q5;
            {var subQ0=sQuery(id+"F20.wireOp",EDGE,"E87");var subQ1=makeQuery(id+"F20.imprint","IMPRINT",EDGE,{"derivedFrom":subQ0});Q5=makeQuery(id+"F22.opExtrude","CAP_EDGE",EDGE,{"disambiguationData":[OSD([subQ0]),TDD([makeQuery(id+"F21.imprint","IMPRINT",EDGE,{"disambiguationData":[TD([[makeQuery(id+"F21.imprint","INTERSECT",VERTEX,{"derivedFrom":[subQ1,sQuery(id+"F21.wireOp",EDGE,"E94.22.0")]}),-1.0]])],"derivedFrom":subQ1})])],"isStart":false});}
            var Q6;
            {var subQ0=sQuery(id+"F20.wireOp",EDGE,"E87");var subQ1=makeQuery(id+"F20.imprint","IMPRINT",EDGE,{"derivedFrom":subQ0});Q6=makeQuery(id+"F22.opExtrude","CAP_EDGE",EDGE,{"disambiguationData":[OSD([subQ0]),TDD([makeQuery(id+"F21.imprint","IMPRINT",EDGE,{"disambiguationData":[TD([[makeQuery(id+"F21.imprint","INTERSECT",VERTEX,{"derivedFrom":[subQ1,sQuery(id+"F21.wireOp",EDGE,"E94.23.0")]}),-1.0]])],"derivedFrom":subQ1})])],"isStart":false});}
            var Q7;
            {var subQ0=sQuery(id+"F20.wireOp",EDGE,"E87");var subQ1=makeQuery(id+"F20.imprint","IMPRINT",EDGE,{"derivedFrom":subQ0});Q7=makeQuery(id+"F22.opExtrude","CAP_EDGE",EDGE,{"disambiguationData":[OSD([subQ0]),TDD([makeQuery(id+"F21.imprint","IMPRINT",EDGE,{"disambiguationData":[TD([[makeQuery(id+"F21.imprint","INTERSECT",VERTEX,{"derivedFrom":[subQ1,sQuery(id+"F21.wireOp",EDGE,"E90")]}),1.0]])],"derivedFrom":subQ1})])],"isStart":false});}
            var Q8;
            {var subQ0=sQuery(id+"F20.wireOp",EDGE,"E87");var subQ1=makeQuery(id+"F20.imprint","IMPRINT",EDGE,{"derivedFrom":subQ0});Q8=makeQuery(id+"F22.opExtrude","CAP_EDGE",EDGE,{"disambiguationData":[OSD([subQ0]),TDD([makeQuery(id+"F21.imprint","IMPRINT",EDGE,{"disambiguationData":[TD([[makeQuery(id+"F21.imprint","INTERSECT",VERTEX,{"derivedFrom":[subQ1,sQuery(id+"F21.wireOp",EDGE,"E94.1.0")]}),-1.0]])],"derivedFrom":subQ1})])],"isStart":false});}
            var Q9;
            {var subQ0=sQuery(id+"F20.wireOp",EDGE,"E87");var subQ1=makeQuery(id+"F20.imprint","IMPRINT",EDGE,{"derivedFrom":subQ0});Q9=makeQuery(id+"F22.opExtrude","CAP_EDGE",EDGE,{"disambiguationData":[OSD([subQ0]),TDD([makeQuery(id+"F21.imprint","IMPRINT",EDGE,{"disambiguationData":[TD([[makeQuery(id+"F21.imprint","INTERSECT",VERTEX,{"derivedFrom":[subQ1,sQuery(id+"F21.wireOp",EDGE,"E94.2.0")]}),-1.0]])],"derivedFrom":subQ1})])],"isStart":false});}
            fillet(context, id + "F24", {"entities" : qUnion([Q0, Q1, Q2, Q3, Q4, Q5, Q6, Q7, Q8, Q9]), "radius" : 15 * mm, "tangentPropagation" : true, "allowEdgeOverflow" : false});
        }
        {
            var Q0;
            Q0=makeQuery(id+"F1.opRevolve","SWEPT_EDGE",EDGE,{"disambiguationData":[OSD([sQuery(id+"F0.wireOp",EDGE,"E7"),sQuery(id+"F0.wireOp",EDGE,"E8")])]});
            var Q1;
            Q1=makeQuery(id+"F1.opRevolve","SWEPT_EDGE",EDGE,{"disambiguationData":[OSD([sQuery(id+"F0.wireOp",EDGE,"E8"),sQuery(id+"F0.wireOp",EDGE,"E9")])]});
            var Q2;
            Q2=makeQuery(id+"F1.opRevolve","SWEPT_EDGE",EDGE,{"disambiguationData":[OSD([sQuery(id+"F0.wireOp",EDGE,"E3"),sQuery(id+"F0.wireOp",EDGE,"E4")])]});
            var Q3;
            Q3=makeQuery(id+"F1.opRevolve","SWEPT_EDGE",EDGE,{"disambiguationData":[OSD([sQuery(id+"F0.wireOp",EDGE,"E4"),sQuery(id+"F0.wireOp",EDGE,"E5")])]});
            fillet(context, id + "F25", {"entities" : qUnion([Q0, Q1, Q2, Q3]), "radius" : .4 * mm, "tangentPropagation" : true, "allowEdgeOverflow" : false});
        }
        {
            var Q0;
            Q0=makeQuery(id+"F11.opExtrude","CAP_FACE",FACE,{"disambiguationData":[OSD([sQuery(id+"F10.wireOp",EDGE,"E60"),sQuery(id+"F10.wireOp",EDGE,"E62"),sQuery(id+"F10.wireOp",EDGE,"E68"),sQuery(id+"F10.wireOp",EDGE,"E69")])],"isStart":false});
            var Q1;
            Q1=makeQuery(id+"F11.opExtrude","CAP_FACE",FACE,{"disambiguationData":[OSD([sQuery(id+"F10.wireOp",EDGE,"E65.MirrorCS"),sQuery(id+"F10.wireOp",EDGE,"E66.MirrorCS"),sQuery(id+"F10.wireOp",EDGE,"E68"),sQuery(id+"F10.wireOp",EDGE,"E69")])],"isStart":false});
            extrude(context, id + "F26", {"entities" : qUnion([Q0, Q1]), "operationType" : NewBodyOperationType.REMOVE, "oppositeDirection" : true, "depth" : 3 * mm});
        }
        {
            var Q0;
            Q0=makeQuery(id+"F0.imprint","IMPRINT",FACE,{"disambiguationData":[TD([[makeQuery(id+"F0.imprint","IMPRINT",EDGE,{"derivedFrom":sQuery(id+"F0.wireOp",EDGE,"E12")}),1.0]])]});
            var Q1;
            Q1=makeQuery(id+"F17.boolean.opBoolean","INTERSECT",EDGE,{"derivedFrom":[makeQuery(id+"F17.opExtrude","SWEPT_FACE",FACE,{"disambiguationData":[OSD([sQuery(id+"F16.wireOp",EDGE,"E74")])]}),makeQuery(id+"F17.opExtrude","SWEPT_FACE",FACE,{"disambiguationData":[OSD([sQuery(id+"F16.wireOp",EDGE,"E79.MirrorCS")])]})]});
            revolve(context, id + "F27", {"operationType" : NewBodyOperationType.ADD, "entities" : qUnion([Q0]), "axis" : qUnion([Q1]), "revolveType" : RevolveType.FULL});
        }
        {
            var Q0;
            Q0=makeQuery(id+"F26.boolean.opBoolean","COPY",EDGE,{"derivedFrom":makeQuery(id+"F26.opExtrude","CAP_EDGE",EDGE,{"disambiguationData":[OSD([sQuery(id+"F0.wireOp",EDGE,"E16"),sQuery(id+"F10.wireOp",EDGE,"E60"),sQuery(id+"F10.wireOp",EDGE,"E62"),sQuery(id+"F10.wireOp",EDGE,"E68"),sQuery(id+"F10.wireOp",EDGE,"E69")])],"isStart":false})});
            var Q1;
            Q1=makeQuery(id+"F11.opExtrude","CAP_EDGE",EDGE,{"disambiguationData":[OSD([sQuery(id+"F10.wireOp",EDGE,"E60")])],"isStart":true});
            var Q2;
            {var subQ0=sQuery(id+"F16.wireOp",EDGE,"E74");var subQ1=sQuery(id+"F16.wireOp",EDGE,"E75");Q2=makeQuery(id+"F17.boolean.opBoolean","COPY",EDGE,{"disambiguationData":[TD([makeQuery(id+"F3.opExtrude","SWEPT_FACE",FACE,{"disambiguationData":[OSD([sQuery(id+"F2.wireOp",EDGE,"E38")])]})])],"derivedFrom":makeQuery(id+"F17.opExtrude","SWEPT_EDGE",EDGE,{"disambiguationData":[OSD([subQ0,subQ1])]})});}
            var Q3;
            {var subQ0=sQuery(id+"F16.wireOp",EDGE,"E74");var subQ1=sQuery(id+"F16.wireOp",EDGE,"E75");Q3=makeQuery(id+"F17.boolean.opBoolean","COPY",EDGE,{"disambiguationData":[TD([makeQuery(id+"F3.opExtrude","SWEPT_FACE",FACE,{"disambiguationData":[OSD([sQuery(id+"F2.wireOp",EDGE,"E39")])]})])],"derivedFrom":makeQuery(id+"F17.opExtrude","SWEPT_EDGE",EDGE,{"disambiguationData":[OSD([subQ0,subQ1])]})});}
            var Q4;
            {var subQ0=sQuery(id+"F10.wireOp",EDGE,"E66.MirrorCS");var subQ1=sQuery(id+"F0.wireOp",EDGE,"E14");var subQ3=sQuery(id+"F0.wireOp",EDGE,"E13");Q4=makeQuery(id+"F17.boolean.opBoolean","SPLIT",EDGE,{"disambiguationData":[TD([makeQuery(id+"F13.opFillet","BLEND_FACE",FACE,{"disambiguationData":[OSD([subQ0,sQuery(id+"F10.wireOp",EDGE,"E69")])]})])],"derivedFrom":makeQuery(id+"F11.boolean.opBoolean","SPLIT",EDGE,{"disambiguationData":[TD([makeQuery(id+"F11.opExtrude","SWEPT_FACE",FACE,{"disambiguationData":[OSD([sQuery(id+"F10.wireOp",EDGE,"E60")])]})])],"derivedFrom":makeQuery(id+"F1.opRevolve","SWEPT_EDGE",EDGE,{"disambiguationData":[OSD([subQ3,subQ1])]})})});}
            var Q5;
            Q5=makeQuery(id+"F13.opFillet","BLEND_EDGE",EDGE,{"blendedFrom":[makeQuery(id+"F11.opExtrude","SWEPT_EDGE",EDGE,{"disambiguationData":[OSD([sQuery(id+"F10.wireOp",EDGE,"E66.MirrorCS"),sQuery(id+"F10.wireOp",EDGE,"E69")])]}),makeQuery(id+"F1.opRevolve","SWEPT_FACE",FACE,{"disambiguationData":[OSD([sQuery(id+"F0.wireOp",EDGE,"E13")])]})],"blendedInto":[makeQuery(id+"F1.opRevolve","SWEPT_FACE",FACE,{"disambiguationData":[OSD([sQuery(id+"F0.wireOp",EDGE,"E13")])]})]});
            var Q6;
            Q6=makeQuery(id+"F26.boolean.opBoolean","COPY",EDGE,{"derivedFrom":makeQuery(id+"F26.opExtrude","CAP_EDGE",EDGE,{"disambiguationData":[OSD([sQuery(id+"F0.wireOp",EDGE,"E16"),sQuery(id+"F10.wireOp",EDGE,"E65.MirrorCS"),sQuery(id+"F10.wireOp",EDGE,"E66.MirrorCS"),sQuery(id+"F10.wireOp",EDGE,"E68"),sQuery(id+"F10.wireOp",EDGE,"E69")])],"isStart":false})});
            var Q7;
            Q7=makeQuery(id+"F11.opExtrude","CAP_EDGE",EDGE,{"disambiguationData":[OSD([sQuery(id+"F10.wireOp",EDGE,"E65.MirrorCS")])],"isStart":true});
            var Q8;
            {var subQ0=sQuery(id+"F16.wireOp",EDGE,"E79.MirrorCS");var subQ1=sQuery(id+"F16.wireOp",EDGE,"E78.MirrorCS");Q8=makeQuery(id+"F17.boolean.opBoolean","COPY",EDGE,{"disambiguationData":[TD([makeQuery(id+"F3.opExtrude","SWEPT_FACE",FACE,{"disambiguationData":[OSD([sQuery(id+"F2.wireOp",EDGE,"E39")])]})])],"derivedFrom":makeQuery(id+"F17.opExtrude","SWEPT_EDGE",EDGE,{"disambiguationData":[OSD([subQ1,subQ0])]})});}
            var Q9;
            {var subQ0=sQuery(id+"F16.wireOp",EDGE,"E78.MirrorCS");var subQ1=sQuery(id+"F16.wireOp",EDGE,"E79.MirrorCS");Q9=makeQuery(id+"F17.boolean.opBoolean","COPY",EDGE,{"disambiguationData":[TD([makeQuery(id+"F3.opExtrude","SWEPT_FACE",FACE,{"disambiguationData":[OSD([sQuery(id+"F2.wireOp",EDGE,"E38")])]})])],"derivedFrom":makeQuery(id+"F17.opExtrude","SWEPT_EDGE",EDGE,{"disambiguationData":[OSD([subQ0,subQ1])]})});}
            var Q10;
            Q10=makeQuery(id+"F11.opExtrude","CAP_EDGE",EDGE,{"disambiguationData":[OSD([sQuery(id+"F10.wireOp",EDGE,"E62")])],"isStart":true});
            var Q11;
            Q11=makeQuery(id+"F1.opRevolve","SWEPT_EDGE",EDGE,{"disambiguationData":[OSD([sQuery(id+"F0.wireOp",EDGE,"E10"),sQuery(id+"F0.wireOp",EDGE,"E11")])]});
            var Q12;
            Q12=makeQuery(id+"F27.opRevolve","SWEPT_EDGE",EDGE,{"disambiguationData":[OSD([sQuery(id+"F0.wireOp",EDGE,"E35"),sQuery(id+"F0.wireOp",EDGE,"E36")])]});
            var Q13;
            Q13=makeQuery(id+"F27.opRevolve","SWEPT_EDGE",EDGE,{"disambiguationData":[OSD([sQuery(id+"F0.wireOp",EDGE,"E36"),sQuery(id+"F0.wireOp",EDGE,"E37")])]});
            fillet(context, id + "F28", {"entities" : qUnion([Q0, Q1, Q2, Q3, Q4, Q5, Q6, Q7, Q8, Q9, Q10, Q11, Q12, Q13]), "radius" : .5 * mm, "tangentPropagation" : true, "allowEdgeOverflow" : false});
        }
    });
